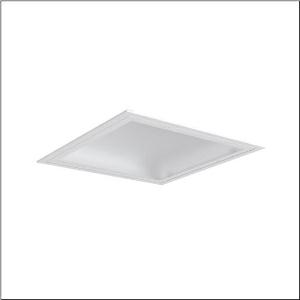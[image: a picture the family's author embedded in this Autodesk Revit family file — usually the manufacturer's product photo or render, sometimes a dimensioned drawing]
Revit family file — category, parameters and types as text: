
# Revit family: mira_r__21_51fr427a462a_66f5
name_source: partatom
category: Lighting Fixtures
units: mm (PartAtom-declared; Revit-internal decimal feet)

## family parameters
Cut with Voids When Loaded = No
Host = Face
Light Source = No
Part Type = Normal
Room Calculation Point = No
Round Connector Dimension = Use Diameter
Shared = No

## types (1)
- Mira® 21 (1 x LED, 6420 lm, 53 W, 4000K)
    Apparent Load = 53 VA
    CIE Flux Codes = 50 81 97 100 100
    Color Rendering = 80
    Color Temperature = 4000K
    Default Elevation = 1800 mm
    Description = Mira® 21, clean room luminaire, primary light control with reflector, primary optical cover: cover, of PC, light emission: direct distribution, primary light characteristic: symmetric, installation type: recessed, LED, rated luminous flux: 6.420lm, luminous efficacy: 121lm/W, light colour: 840, colour temperature: 4000K, control gear: ECG, with terminal, 3-pole, max. 2.5mm², mains connection: 230V, AC, 50/60Hz, rated input power: 53W, luminaire housing, of sheet steel, coated, pure white (RAL 9010), with concealed spring brackets, module: M625, length: 623mm, width: 623mm, height: 115mm, protection rating (complete): IP54, insulation class (complete): insulation class I (protective earthing), certification: CE, UKCA, permissible operating ambient temperature: -5..+40°C, standard: EN 50419, packaging unit: 1 piece
    Height = 0 mm  [stored 0 ft]
    Lamp = 1 x LED
    Lamp Light Flux = 6420 lm
    Lamp Power = 53 W
    Lamp count = 1
    Length = 625 mm
    Luminous efficacy = 121 lm/W
    Manufacturer = Siteco
    ModVariant = No
    Model = 51FR427A462A
    Mounting Place = Ceiling
    Mounting Type = Recessed
    Number of Poles = 1
    OnlyDefault = Yes
    Power Factor = 1
    Product Name = Mira® 21
    Product group = clean room luminaire
    ProductGroupID = 402
    Protection Class = Protection class I
    Protection Degree = IP 54
    RLX_Detail_Level = 1
    RLX_Emergency_Light_Flux = 0 lm
    RLX_Emergency_Type = 0
    RLX_Emergency_Type_DB = No
    RlxData = <blob elided: 13377 chars, md5=e283aa77>
    Socket = socket
    Standby Power = 0 W
    System Light Flux = 6420 lm
    System Power = 53 W
    Type Comments = Product without accessories
    Type Image = l_1007109.jpg
    URL = http://relux.com
    VarID = ---
    Voltage = 0 V
    Weight = 0.00 kg
    Width = 625 mm

note: [stored X ft] marks values corroborated as IEEE doubles in the binary element streams (Revit-internal decimal feet)

## geometry (parser evidence)
native form markers: Sweep x9
no freeform markers — native parametric forms only
